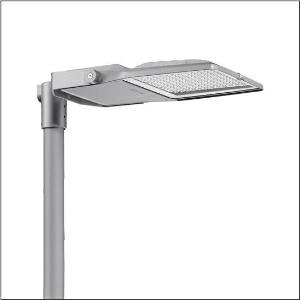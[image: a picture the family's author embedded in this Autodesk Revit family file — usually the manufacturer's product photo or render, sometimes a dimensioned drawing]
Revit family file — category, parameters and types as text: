
# Revit family: floodlight_fl_21_iq_midi___pl33t_5xa7781e4f3a_bb4e
name_source: partatom
category: Lighting Fixtures
units: mm (PartAtom-declared; Revit-internal decimal feet)

## family parameters
Cut with Voids When Loaded = No
Host = Face
Light Source = No
Part Type = Normal
Room Calculation Point = No
Round Connector Dimension = Use Diameter
Shared = No

## types (1)
- --- (1 x LED, 27690 lm, 208.1 W, 4000K)
    Apparent Load = 208 VA
    CIE Flux Codes = 26 75 99 100 100
    Color Rendering = 70
    Color Temperature = 4000K
    Default Elevation = 1800 mm
    Description = Floodlight FL 21 iQ midi, floodlight, primary light control with lens, of PMMA, primary optical cover: protective disc, of toughened safety glass, transparent, light distribution: PL33T, light emission: direct distribution, installation type: surface-mounted, LED, High Power LED, rated luminous flux: 27.690lm, luminous efficacy: 133lm/W, light colour: 740, colour temperature: 4000K, control gear: ECG iQ, control: optimised constant luminous flux control (CLO 2.0), Desk-Remote (wireless, voltage-free reading and setting of iQ features in the workshop via application-optimized NFC function/RFID function), Light-Fading, Smart-Wire, Night-Set, Lumen-Switch, Temp-Guard, Auto-Match, with terminal, 6-pole, mains connection: 220..240V, AC, 50/60Hz, start of lifetime: 208W, end of service life: 227W, reduction: 90W, luminaire housing, of diecast aluminium, powder-coated, Siteco® metallic grey (DB 702S), corrosivity category C5 mid according to DIN EN ISO 12944, sealing non-destructively replaceable, please order mast flange separately, mast bracket, of steel, galvanised, powder-coated, Siteco® metallic grey (DB 702S), protection rating (complete): IP66, insulation class (complete): insulation class II (safety insulation), certification: CE, ENEC, VDE, protection symbol: D, impact resistance: IK08, permissible operating ambient temperature: -40..+40°C, permissible operating ambient temperature for outdoor applications: -40..+50°C, standard: DIN EN 12944, LABS conformity tested according to VDMA 24364:2018-05, packaging unit: 1 piece

Light Distribution: PL33T
    Height = 76 mm
    Lamp = 1 x LED
    Lamp Light Flux = 27690 lm
    Lamp Power = 208.1 W
    Lamp count = 1
    Length = 657 mm
    Luminous efficacy = 133 lm/W
    Manufacturer = Siteco
    ModVariant = No
    Model = 5XA7781E4F3A
    Number of Poles = 1
    OnlyDefault = Yes
    Power Factor = 1
    Product Name = Floodlight FL 21 iQ midi | PL33T
    Product group = floodlight | pylon annexe
    ProductGroupID = 6200
    Protection Class = Protection class II
    Protection Degree = IP 66
    RLX_Detail_Level = 1
    RLX_Emergency_Light_Flux = 0 lm
    RLX_Emergency_Type = 0
    RLX_Emergency_Type_DB = No
    RlxData = <blob elided: 153633 chars, md5=482239f1>
    Socket = socket
    Standby Power = 0 W
    System Light Flux = 27690 lm
    System Power = 208 W
    Type Comments = factory setting: luminous flux: 100 % | dim-lin: 254 | 710 mA
    Type Image = l_1007123.jpg
    URL = http://relux.com
    VarID = @adj_072791
    Voltage = 0 V
    Weight = 0.00 kg
    Width = 442 mm

## geometry (parser evidence)
native form markers: Blend x4, Sweep x14
no freeform markers — native parametric forms only
